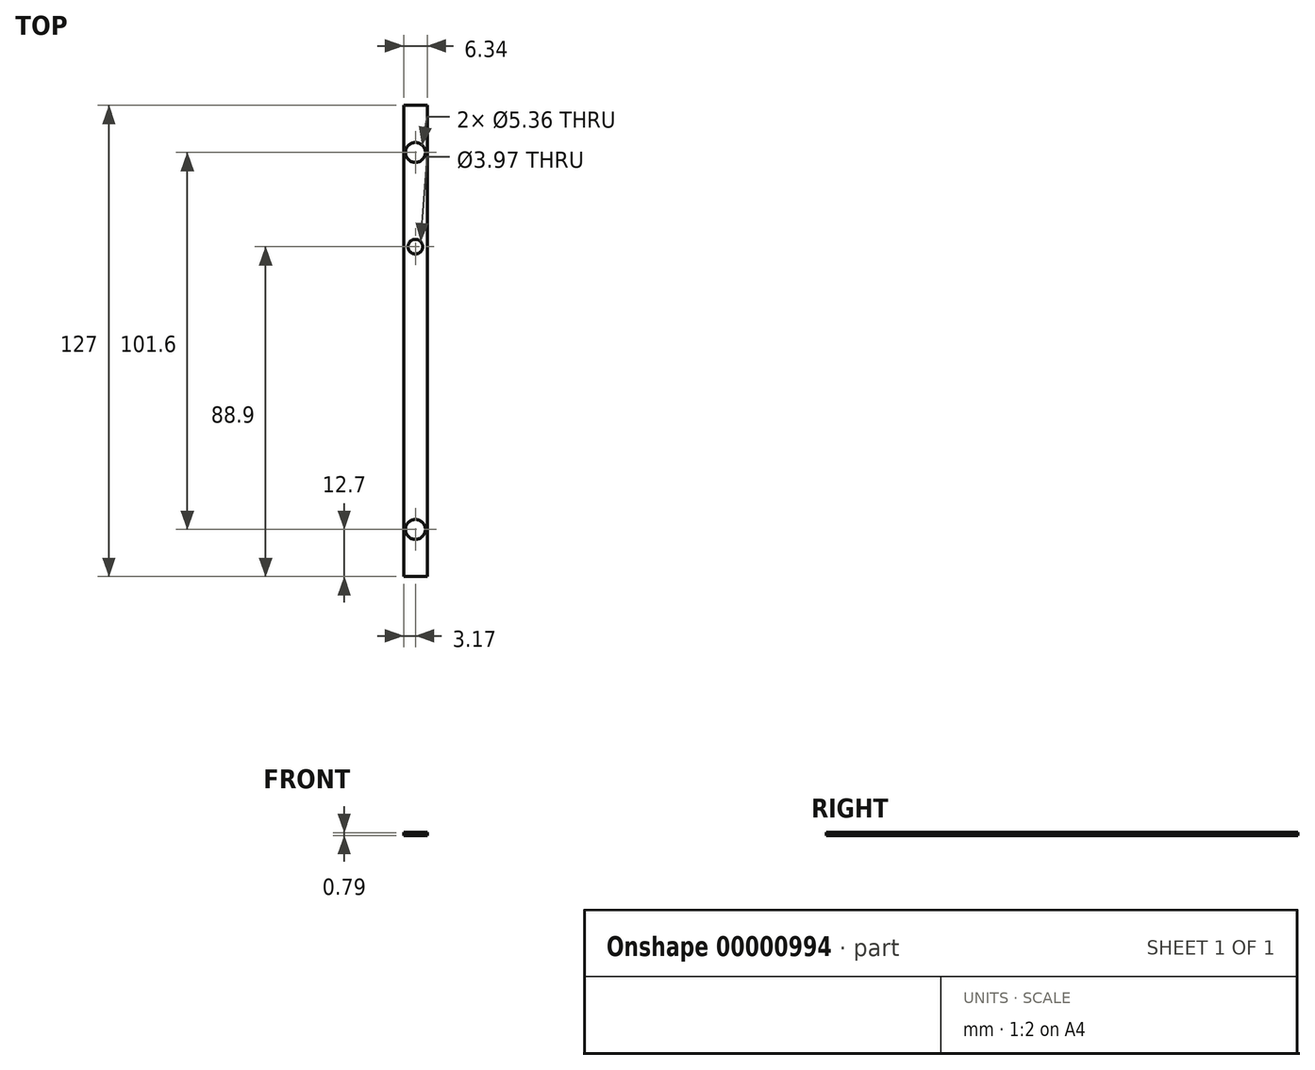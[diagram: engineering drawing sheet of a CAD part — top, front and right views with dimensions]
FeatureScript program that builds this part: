
annotation { "Feature Type Name" : "Feature", "Feature Type Description" : "" }
export const myFeature = defineFeature(function(context is Context, id is Id, definition is map)
    precondition{}
    {
        {
            var Q0;
            Q0=qCreatedBy(makeId("Top.planeOp"),FACE);
            var sketch = newSketch(context, id + "F0", { "sketchPlane" : qUnion([Q0])});
            skLineSegment(sketch, "E0.rect.bottom", {"start": v(3.17, 63.5) * mm, "end": v(-3.18, 63.5) * mm});
            skLineSegment(sketch, "E0.rect.top", {"start": v(3.17, -63.5) * mm, "end": v(-3.18, -63.5) * mm});
            skLineSegment(sketch, "E0.rect.left", {"start": v(3.17, 63.5) * mm, "end": v(3.17, -63.5) * mm});
            skLineSegment(sketch, "E0.rect.right", {"start": v(-3.18, 63.5) * mm, "end": v(-3.18, -63.5) * mm});
            skPoint(sketch, "E0.rect.middle", {"position": v(0, 0) * mm});
            skCircle(sketch, "E1", {"center": v(0, 50.8) * mm, "radius": 2.68 * mm});
            skCircle(sketch, "E2", {"center": v(0, -50.8) * mm, "radius": 2.68 * mm});
            skCircle(sketch, "E3", {"center": v(0, 25.4) * mm, "radius": 1.98 * mm});
            skSolve(sketch);
        }
        {
            var Q0;
            Q0=makeQuery(id+"F0.imprint","IMPRINT",FACE,{"disambiguationData":[TD([[makeQuery(id+"F0.imprint","IMPRINT",EDGE,{"derivedFrom":sQuery(id+"F0.wireOp",EDGE,"E0.rect.bottom")}),1.0]])]});
            extrude(context, id + "F1", {"entities" : qUnion([Q0]), "depth" : 0.8 * mm});
        }
    });
